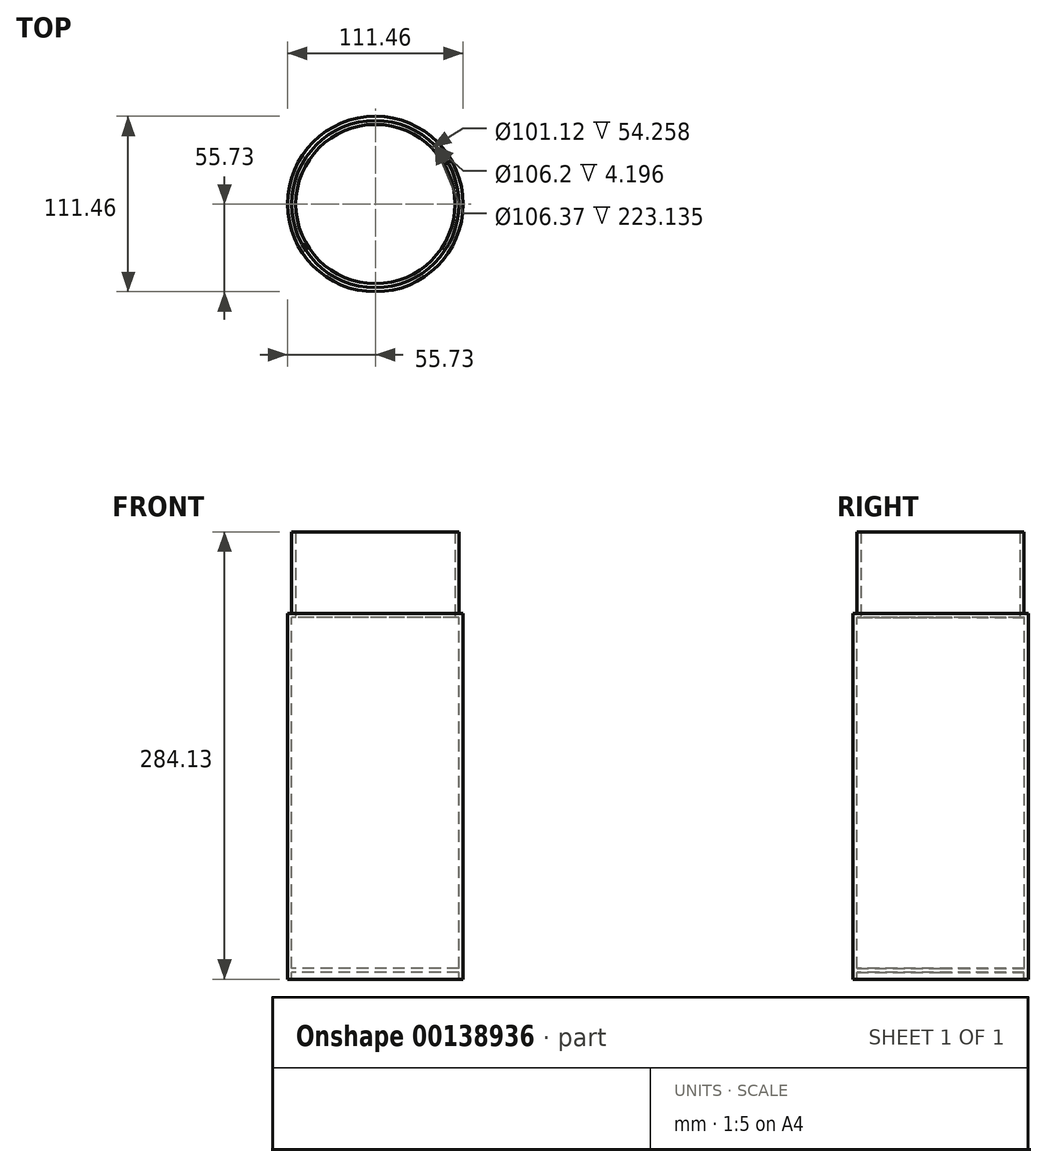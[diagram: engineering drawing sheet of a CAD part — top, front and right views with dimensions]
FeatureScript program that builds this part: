
annotation { "Feature Type Name" : "Feature", "Feature Type Description" : "" }
export const myFeature = defineFeature(function(context is Context, id is Id, definition is map)
    precondition{}
    {
        {
            var Q0;
            Q0=qCreatedBy(makeId("Top.planeOp"),FACE);
            var sketch = newSketch(context, id + "F0", { "sketchPlane" : qUnion([Q0])});
            skCircle(sketch, "E0", {"center": v(0, 0) * mm, "radius": 55.73 * mm});
            skCircle(sketch, "E1", {"center": v(0, 0) * mm, "radius": 53.1 * mm});
            skSolve(sketch);
        }
        {
            var Q0;
            Q0=makeQuery(id+"F0.imprint","IMPRINT",FACE,{"disambiguationData":[TD([[makeQuery(id+"F0.imprint","IMPRINT",EDGE,{"derivedFrom":sQuery(id+"F0.wireOp",EDGE,"E1")}),1.0]])]});
            extrude(context, id + "F1", {"entities" : qUnion([Q0]), "depth" : 51.72 * mm});
        }
        {
            var Q0;
            Q0=makeQuery(id+"F0.imprint","IMPRINT",FACE,{"disambiguationData":[TD([[makeQuery(id+"F0.imprint","IMPRINT",EDGE,{"derivedFrom":sQuery(id+"F0.wireOp",EDGE,"E0")}),1.0]])]});
            var Q1;
            Q1=sQuery(id+"F0.wireOp",EDGE,"E0");
            var Q2;
            Q2=sQuery(id+"F0.wireOp",EDGE,"E1");
            extrude(context, id + "F2", {"entities" : qUnion([Q0]), "surfaceEntities" : qUnion([Q1, Q2]), "oppositeDirection" : true, "depth" : 232.4 * mm});
        }
        {
            var Q0;
            Q0=makeQuery(id+"F1.opExtrude","CAP_FACE",FACE,{"disambiguationData":[OSD([sQuery(id+"F0.wireOp",EDGE,"E1")])],"isStart":false});
            shell(context, id + "F3", {"entities" : qUnion([Q0]), "thickness" : 2.54 * mm});
        }
        {
            var Q0;
            Q0=makeQuery(id+"F1.opExtrude","CAP_FACE",FACE,{"disambiguationData":[OSD([sQuery(id+"F0.wireOp",EDGE,"E1")])],"isStart":true});
            extrude(context, id + "F4", {"entities" : qUnion([Q0]), "operationType" : NewBodyOperationType.ADD, "depth" : 228.21 * mm});
        }
        {
            var Q0;
            {var subQ0=sQuery(id+"F0.wireOp",EDGE,"E1");Q0=makeQuery(id+"F3.opShell","OFFSET_FACE",FACE,{"disambiguationData":[OSD([subQ0]),TDD([makeQuery(id+"F1.opExtrude","CAP_FACE",FACE,{"disambiguationData":[OSD([subQ0])],"isStart":true})])]});}
            shell(context, id + "F5", {"entities" : qUnion([Q0]), "thickness" : 2.54 * mm});
        }
    });
